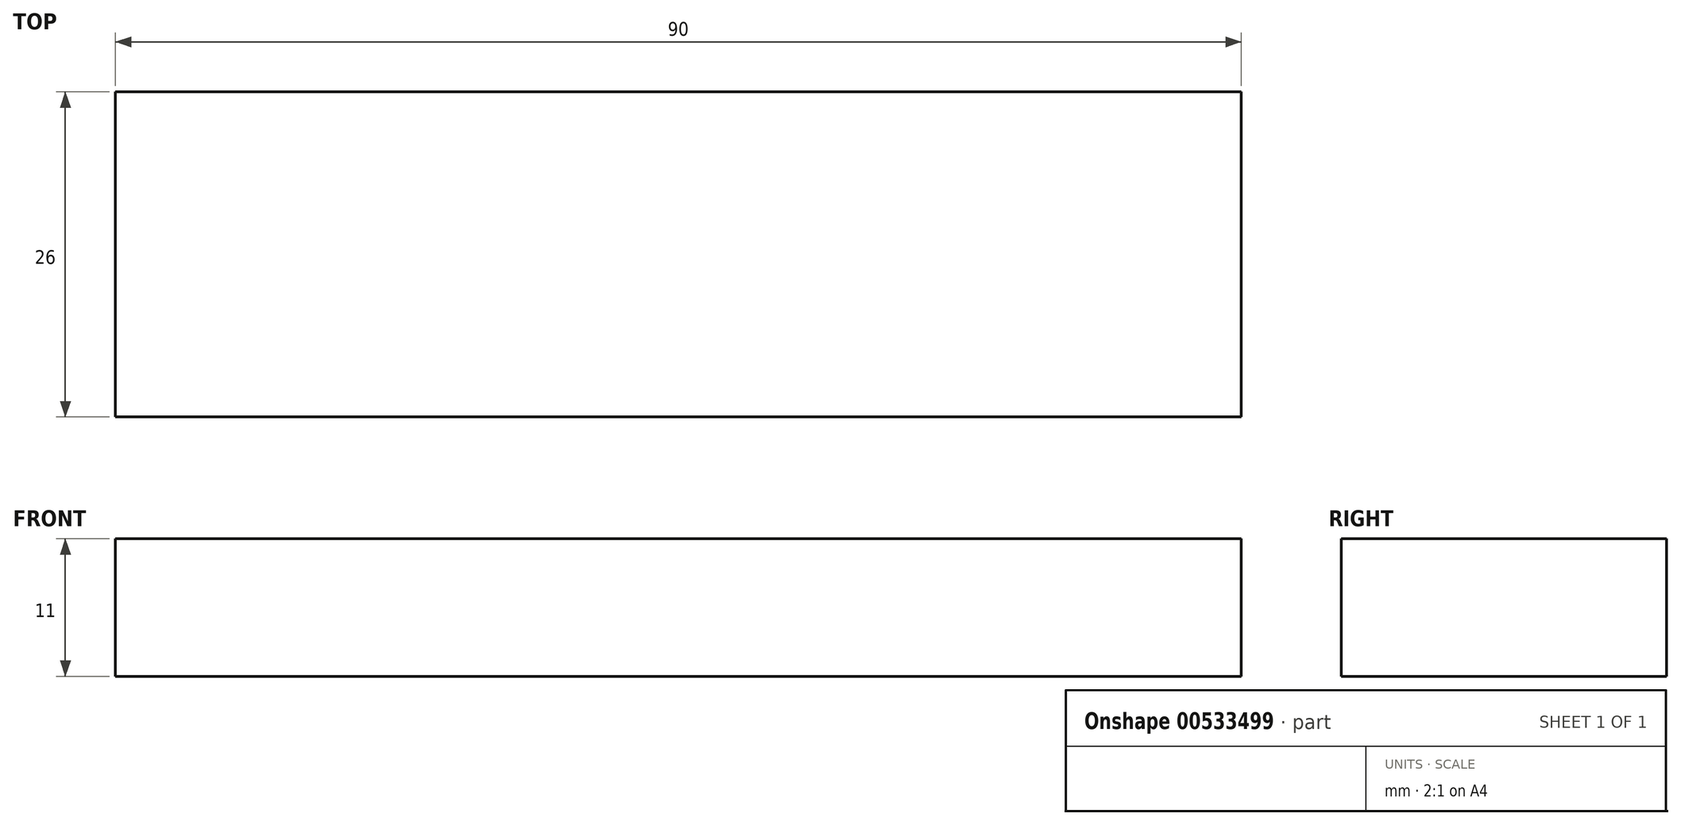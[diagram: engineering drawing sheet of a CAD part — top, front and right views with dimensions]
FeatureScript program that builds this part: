
annotation { "Feature Type Name" : "Feature", "Feature Type Description" : "" }
export const myFeature = defineFeature(function(context is Context, id is Id, definition is map)
    precondition{}
    {
        {
            var Q0;
            Q0=qCreatedBy(makeId("Top.planeOp"),FACE);
            var sketch = newSketch(context, id + "F0", { "sketchPlane" : qUnion([Q0])});
            skLineSegment(sketch, "E0.bottom", {"start": v(0, 0) * mm, "end": v(90, 0) * mm});
            skLineSegment(sketch, "E0.top", {"start": v(0, 26) * mm, "end": v(90, 26) * mm});
            skLineSegment(sketch, "E0.left", {"start": v(0, 0) * mm, "end": v(0, 26) * mm});
            skLineSegment(sketch, "E0.right", {"start": v(90, 0) * mm, "end": v(90, 26) * mm});
            skSolve(sketch);
        }
        {
            var Q0;
            Q0=qSketchRegion(id+"F0",true);
            extrude(context, id + "F1", {"entities" : qUnion([Q0]), "depth" : 11 * mm, "offsetDistance" : 25 * mm});
        }
    });
